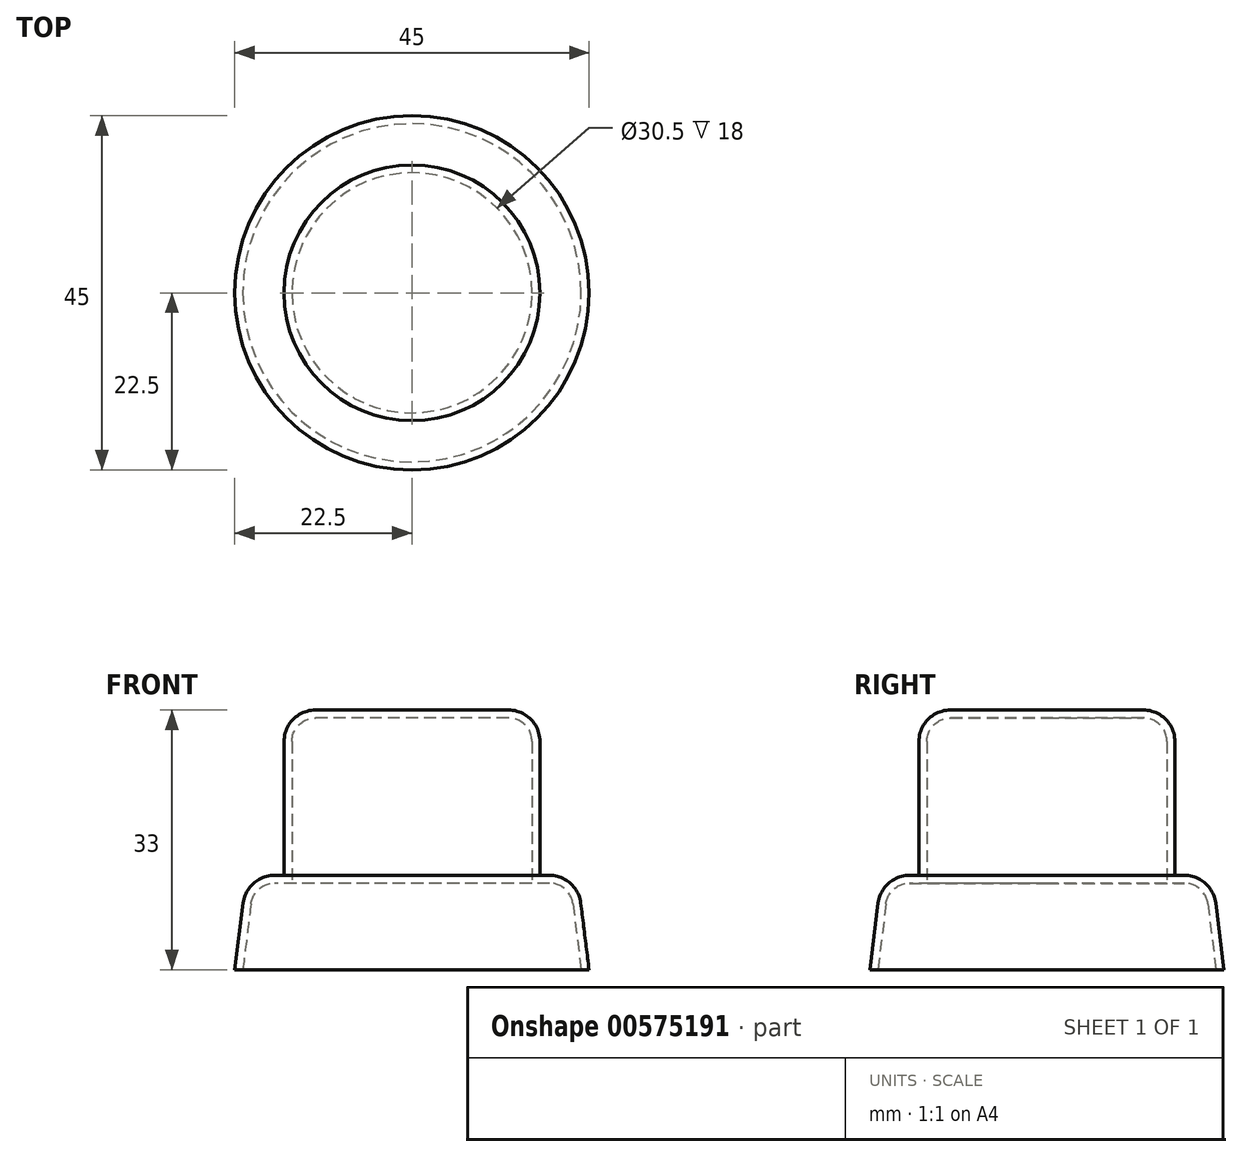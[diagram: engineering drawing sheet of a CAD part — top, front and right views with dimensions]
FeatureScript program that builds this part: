
annotation { "Feature Type Name" : "Feature", "Feature Type Description" : "" }
export const myFeature = defineFeature(function(context is Context, id is Id, definition is map)
    precondition{}
    {
        {
            var Q0;
            Q0=qCreatedBy(makeId("Top.planeOp"),FACE);
            var sketch = newSketch(context, id + "F0", { "sketchPlane" : qUnion([Q0])});
            skCircle(sketch, "E0", {"center": v(0, 0) * mm, "radius": 22.5 * mm});
            skSolve(sketch);
        }
        {
            var Q0;
            Q0=qCreatedBy(makeId("Top.planeOp"),FACE);
            cPlane(context, id + "F1", {"entities" : qUnion([Q0]), "cplaneType" : CPlaneType.OFFSET, "offset" : 12 * mm, "width" : 150 * mm, "height" : 150 * mm});
        }
        {
            var Q0;
            Q0=qCreatedBy(id+"F1.planeOp",FACE);
            var sketch = newSketch(context, id + "F2", { "sketchPlane" : qUnion([Q0])});
            skCircle(sketch, "E1", {"center": v(0, 0) * mm, "radius": 21 * mm});
            skSolve(sketch);
        }
        {
            var Q0;
            Q0=makeQuery(id+"F0.imprint","IMPRINT",FACE,{"disambiguationData":[TD([[makeQuery(id+"F0.imprint","IMPRINT",EDGE,{"derivedFrom":sQuery(id+"F0.wireOp",EDGE,"E0")}),1.0]])]});
            var Q1;
            Q1=makeQuery(id+"F2.imprint","IMPRINT",FACE,{"disambiguationData":[TD([[makeQuery(id+"F2.imprint","IMPRINT",EDGE,{"derivedFrom":sQuery(id+"F2.wireOp",EDGE,"E1")}),1.0]])]});
            loft(context, id + "F3", {"sheetProfilesArray" : [{ "sheetProfileEntities" : qUnion([Q0]) }, { "sheetProfileEntities" : qUnion([Q1]) }]});
        }
        {
            var Q0;
            Q0=makeQuery(id+"F3.opLoft","MID_CAP_EDGE",EDGE,{"disambiguationData":[OSD([sQuery(id+"F0.wireOp",EDGE,"E0"),sQuery(id+"F2.wireOp",EDGE,"E1")])],"capPos":1.0});
            fillet(context, id + "F4", {"entities" : qUnion([Q0]), "radius" : 4 * mm, "tangentPropagation" : true, "allowEdgeOverflow" : false});
        }
        {
            var Q0;
            Q0=makeQuery(id+"F3.opLoft","CAP_FACE",FACE,{"disambiguationData":[OSD([makeQuery(id+"F2.imprint","IMPRINT",FACE,{"disambiguationData":[TD([[makeQuery(id+"F2.imprint","IMPRINT",EDGE,{"derivedFrom":sQuery(id+"F2.wireOp",EDGE,"E1")}),1.0]])]})])],"isStart":true});
            var sketch = newSketch(context, id + "F5", { "sketchPlane" : qUnion([Q0])});
            skCircle(sketch, "E2", {"center": v(0, 0) * mm, "radius": 16.25 * mm});
            skSolve(sketch);
        }
        {
            var Q0;
            Q0 = qSketchRegion(id + "F5", true);
            extrude(context, id + "F6", {"entities" : qUnion([Q0]), "operationType" : NewBodyOperationType.ADD, "depth" : 21 * mm, "offsetDistance" : 25 * mm});
        }
        {
            var Q0;
            Q0=makeQuery(id+"F6.opExtrude","CAP_EDGE",EDGE,{"disambiguationData":[OSD([sQuery(id+"F5.wireOp",EDGE,"E2")])],"isStart":false});
            fillet(context, id + "F7", {"entities" : qUnion([Q0]), "radius" : 4 * mm, "tangentPropagation" : true, "allowEdgeOverflow" : false});
        }
        {
            var Q0;
            Q0=makeQuery(id+"F3.opLoft","CAP_FACE",FACE,{"disambiguationData":[OSD([makeQuery(id+"F0.imprint","IMPRINT",FACE,{"disambiguationData":[TD([[makeQuery(id+"F0.imprint","IMPRINT",EDGE,{"derivedFrom":sQuery(id+"F0.wireOp",EDGE,"E0")}),1.0]])]})])],"isStart":true});
            shell(context, id + "F8", {"entities" : qUnion([Q0]), "thickness" : 1 * mm});
        }
    });
